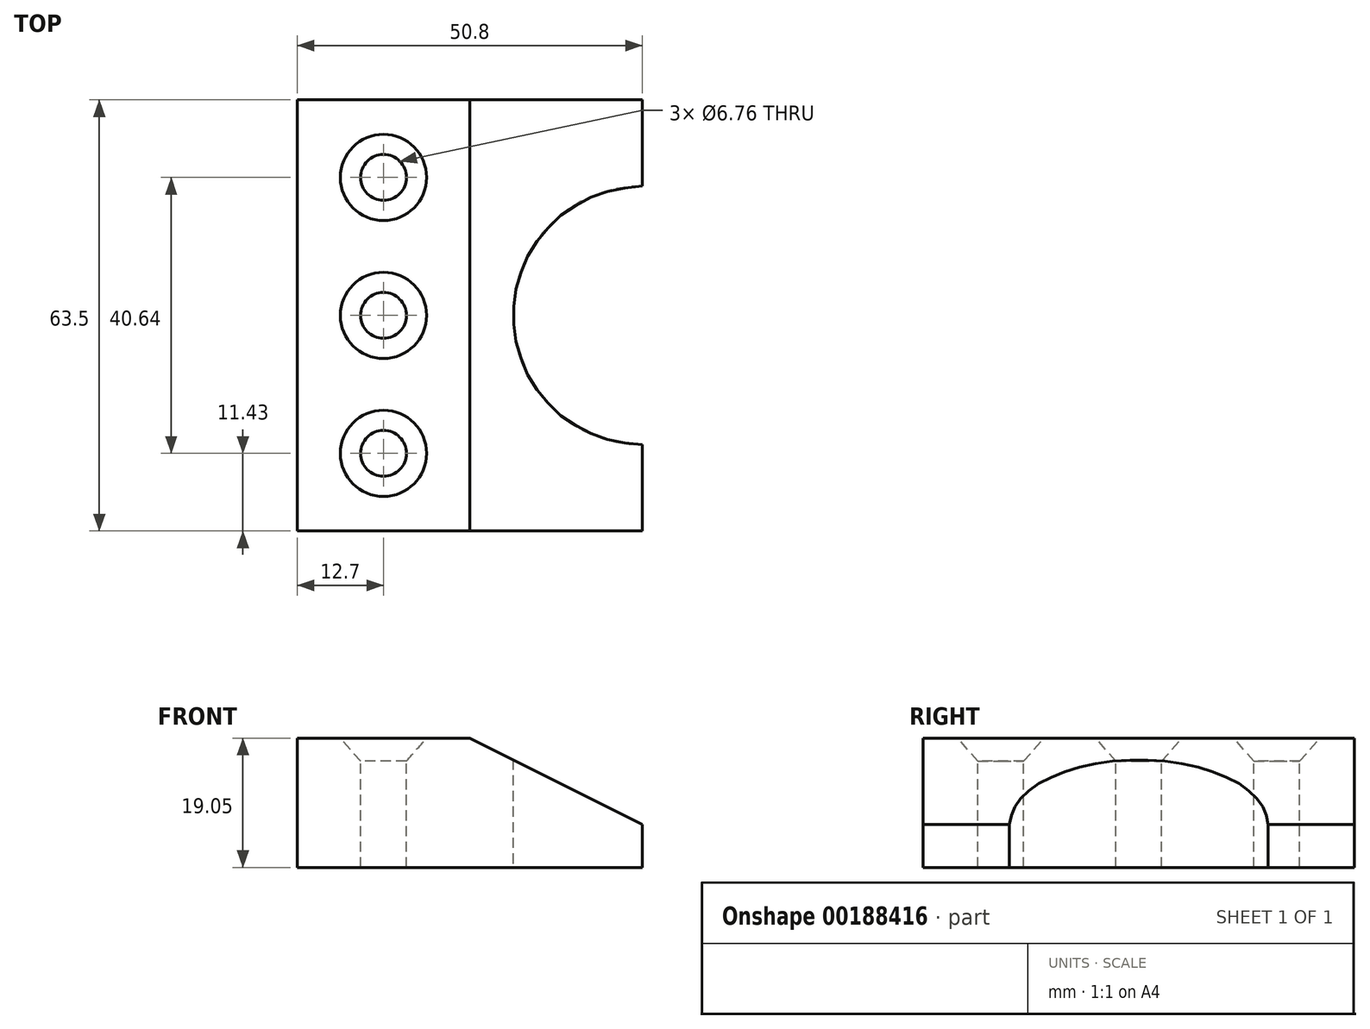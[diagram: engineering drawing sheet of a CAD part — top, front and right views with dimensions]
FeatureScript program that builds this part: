
annotation { "Feature Type Name" : "Feature", "Feature Type Description" : "" }
export const myFeature = defineFeature(function(context is Context, id is Id, definition is map)
    precondition{}
    {
        {
            var Q0;
            Q0=qCreatedBy(makeId("Top.planeOp"),FACE);
            var sketch = newSketch(context, id + "F0", { "sketchPlane" : qUnion([Q0])});
            skLineSegment(sketch, "E0.bottom", {"start": v(0, 0) * mm, "end": v(50.8, 0) * mm});
            skLineSegment(sketch, "E0.top", {"start": v(0, 63.5) * mm, "end": v(50.8, 63.5) * mm});
            skLineSegment(sketch, "E0.left", {"start": v(0, 0) * mm, "end": v(0, 63.5) * mm});
            skLineSegment(sketch, "E0.right", {"start": v(50.8, 0) * mm, "end": v(50.8, 63.5) * mm});
            skLineSegment(sketch, "E1", {"start": v(25.4, 63.5) * mm, "end": v(25.4, 0) * mm});
            skCircle(sketch, "E2", {"center": v(50.8, 31.75) * mm, "radius": 19.05 * mm});
            skPoint(sketch, "E3.orphan", {"position": v(12.7, 63.5) * mm});
            skPoint(sketch, "E4.orphan", {"position": v(12.7, 0) * mm});
            skSolve(sketch);
        }
        {
            var Q0;
            {var subQ1=sQuery(id+"F0.wireOp",EDGE,"E0.left");Q0=makeQuery(id+"F0.imprint","IMPRINT",FACE,{"disambiguationData":[TD([[makeQuery(id+"F0.imprint","IMPRINT",EDGE,{"derivedFrom":subQ1}),-1.0]])]});}
            extrude(context, id + "F1", {"entities" : qUnion([Q0]), "depth" : 19.05 * mm});
        }
        {
            var Q0;
            Q0=makeQuery(id+"F1.opExtrude","SWEPT_FACE",FACE,{"disambiguationData":[OSD([sQuery(id+"F0.wireOp",EDGE,"E1")])]});
            cPlane(context, id + "F2", {"entities" : qUnion([Q0]), "cplaneType" : CPlaneType.OFFSET, "offset" : 25.4 * mm, "width" : 152.4 * mm, "height" : 152.4 * mm});
        }
        {
            var Q0;
            Q0=qCreatedBy(id+"F2.planeOp",FACE);
            var sketch = newSketch(context, id + "F3", { "sketchPlane" : qUnion([Q0])});
            skLineSegment(sketch, "E5.bottom", {"start": v(0, 0) * mm, "end": v(63.5, 0) * mm});
            skLineSegment(sketch, "E5.top", {"start": v(0, 6.35) * mm, "end": v(63.5, 6.35) * mm});
            skLineSegment(sketch, "E5.left", {"start": v(0, 0) * mm, "end": v(0, 6.35) * mm});
            skLineSegment(sketch, "E5.right", {"start": v(63.5, 0) * mm, "end": v(63.5, 6.35) * mm});
            skSolve(sketch);
        }
        {
            var Q1;
            Q1=makeQuery(id+"F1.opExtrude","SWEPT_FACE",FACE,{"disambiguationData":[OSD([sQuery(id+"F0.wireOp",EDGE,"E1")])]});
            var Q2;
            Q2=makeQuery(id+"F3.imprint","IMPRINT",FACE,{"disambiguationData":[TD([[makeQuery(id+"F3.imprint","IMPRINT",EDGE,{"derivedFrom":sQuery(id+"F3.wireOp",EDGE,"E5.bottom")}),1.0]])]});
            loft(context, id + "F4", {"operationType" : NewBodyOperationType.ADD, "sheetProfilesArray" : [{ "sheetProfileEntities" : qUnion([Q1]) }, { "sheetProfileEntities" : qUnion([Q2]) }]});
        }
        {
            var Q0;
            Q0=sQuery(id+"F0.wireOp",VERTEX,"E2.center");
            var Q1;
            Q1=makeQuery(id+"F1.opExtrude","SWEPT_BODY",BODY,{"disambiguationData":[OSD([sQuery(id+"F0.wireOp",EDGE,"E0.bottom"),sQuery(id+"F0.wireOp",EDGE,"E0.top"),sQuery(id+"F0.wireOp",EDGE,"E0.left"),sQuery(id+"F0.wireOp",EDGE,"E1"),sQuery(id+"F0.wireOp",EDGE,"iOJZENtl-hy9J-sDrz-zKsd-4Be4fRd0rM9q"),sQuery(id+"F0.wireOp",EDGE,"O29Pm4mQ-3O6F-owyF-WIio-ay9Mwq0Nx3ni"),sQuery(id+"F0.wireOp",EDGE,"64auMI2L-aL5H-yJHH-0SHF-TEeDZJZdLwfz")])]});
            hole(context, id + "F5", {"style" : HoleStyle.SIMPLE, "endStyle" : HoleEndStyle.THROUGH, "oppositeDirection" : true, "holeDiameter" : 38.1 * mm, "locations" : qUnion([Q0]), "scope" : qUnion([Q1]), "isTappedThrough" : true});
        }
        {
            var Q0;
            Q0=makeQuery(id+"F1.opExtrude","CAP_FACE",FACE,{"disambiguationData":[OSD([sQuery(id+"F0.wireOp",EDGE,"E0.bottom"),sQuery(id+"F0.wireOp",EDGE,"E0.top"),sQuery(id+"F0.wireOp",EDGE,"E0.left"),sQuery(id+"F0.wireOp",EDGE,"E1")])],"isStart":false});
            cPlane(context, id + "F6", {"entities" : qUnion([Q0]), "cplaneType" : CPlaneType.OFFSET, "offset" : 0 * mm, "width" : 152.4 * mm, "height" : 152.4 * mm});
        }
        {
            var Q0;
            Q0=qCreatedBy(id+"F6.planeOp",FACE);
            var sketch = newSketch(context, id + "F7", { "sketchPlane" : qUnion([Q0])});
            skLineSegment(sketch, "E6", {"start": v(0, 0) * mm, "end": v(12.7, 0) * mm});
            skPoint(sketch, "E7", {"position": v(12.7, 52.07) * mm});
            skPoint(sketch, "E8", {"position": v(12.7, 31.75) * mm});
            skPoint(sketch, "E9", {"position": v(12.7, 11.43) * mm});
            skSolve(sketch);
        }
        {
            var Q0;
            Q0=sQuery(id+"F7.wireOp",VERTEX,"E7");
            var Q1;
            Q1=sQuery(id+"F7.wireOp",VERTEX,"E8");
            var Q2;
            Q2=sQuery(id+"F7.wireOp",VERTEX,"E9");
            var Q3;
            Q3=makeQuery(id+"F1.opExtrude","SWEPT_BODY",BODY,{"disambiguationData":[OSD([sQuery(id+"F0.wireOp",EDGE,"E0.bottom"),sQuery(id+"F0.wireOp",EDGE,"E0.top"),sQuery(id+"F0.wireOp",EDGE,"E0.left"),sQuery(id+"F0.wireOp",EDGE,"E1")])]});
            hole(context, id + "F8", {"style" : HoleStyle.C_SINK, "endStyle" : HoleEndStyle.THROUGH, "holeDiameter" : 6.76 * mm, "cSinkDiameter" : 12.7 * mm, "cSinkAngle" : 82 * degree, "locations" : qUnion([Q0, Q1, Q2]), "scope" : qUnion([Q3]), "isTappedThrough" : true});
        }
    });
